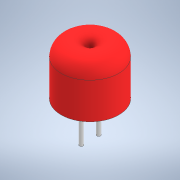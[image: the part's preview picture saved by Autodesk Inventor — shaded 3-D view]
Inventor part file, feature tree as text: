
AUTODESK INVENTOR PART (.ipt)
format: ipt  version: 2021 (Build 250183000, 183)  size: 154,112 bytes
history: native  units: mm
features: sketch x3, revolve x1, extrude x1
ambient origin geometry x8: Origin, YZ Plane, XZ Plane, XY Plane, X Axis, Y Axis, Z Axis, Center Point
bodies: Solid1 (feature_tree)
feature tree (5):
  revolve  "Revolution1"  [1 undecoded]
  sketch  "Sketch2"  dims[d2=4.0mm d3=90.0deg]
  sketch  "Sketch3"  dims[d4=1.0mm d5=1.0mm d6=10.0mm d7=0.0mm d8=4.835078mm]
  extrude  "Extrusion1"  TaperAngle=90.0deg  [1 undecoded]
  sketch  "Sketch1"  dims[d0=8.0mm d1=14.0mm]
note: 2 required parameter values undecoded (feature->parameter linkage not recoverable at this tier; creation-order binding heuristic only, values carry confidence <= 0.55)